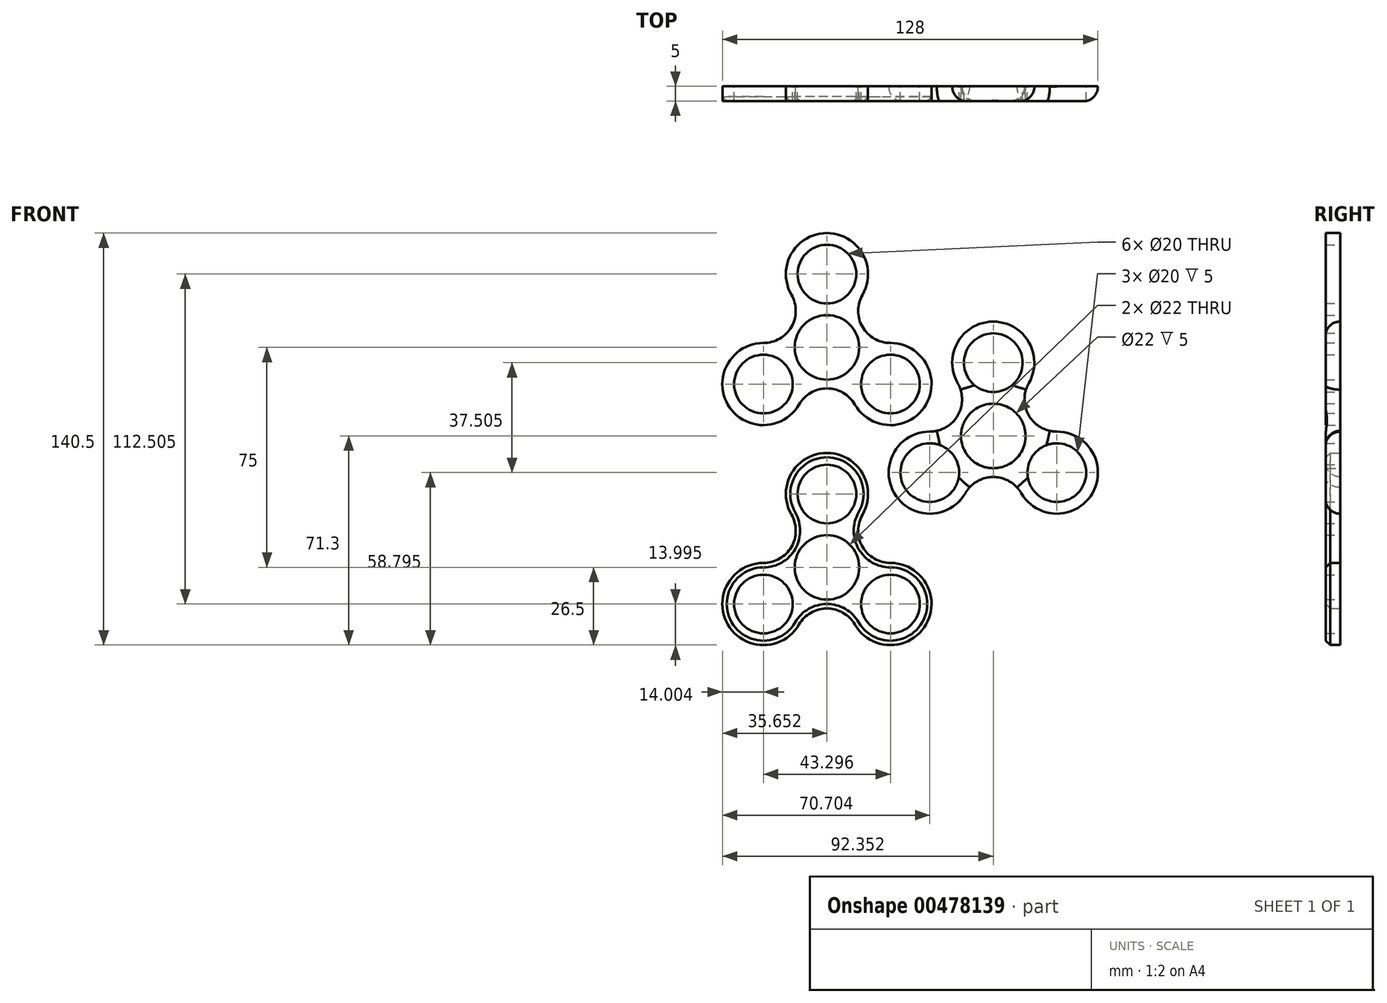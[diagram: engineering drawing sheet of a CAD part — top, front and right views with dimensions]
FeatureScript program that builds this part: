
annotation { "Feature Type Name" : "Feature", "Feature Type Description" : "" }
export const myFeature = defineFeature(function(context is Context, id is Id, definition is map)
    precondition{}
    {
        {
            var Q0;
            Q0=qCreatedBy(makeId("Front.planeOp"),FACE);
            var sketch = newSketch(context, id + "F0", { "sketchPlane" : qUnion([Q0])});
            skCircle(sketch, "E0", {"center": v(16.93, -40.24) * mm, "radius": 39 * mm});
            skCircle(sketch, "E1", {"center": v(16.93, -40.24) * mm, "radius": 11 * mm});
            skArc(sketch, "E2", {"start": v(16.93, -1.24) * mm, "mid": v(-16.84, -20.74) * mm, "end": v(-16.84, -59.75) * mm});
            skArc(sketch, "E3", {"start": v(-16.84, -59.75) * mm, "mid": v(16.93, -79.25) * mm, "end": v(50.7, -59.75) * mm});
            skLineSegment(sketch, "E4", {"start": v(-16.84, -59.75) * mm, "end": v(-13.37, -57.75) * mm});
            skLineSegment(sketch, "E5", {"start": v(16.93, -1.24) * mm, "end": v(16.93, -5.24) * mm});
            skLineSegment(sketch, "E6", {"start": v(50.7, -59.75) * mm, "end": v(47.24, -57.75) * mm});
            skCircle(sketch, "E7", {"center": v(16.93, -15.24) * mm, "radius": 10 * mm});
            skCircle(sketch, "E8", {"center": v(-4.72, -52.74) * mm, "radius": 10 * mm});
            skCircle(sketch, "E9", {"center": v(38.58, -52.74) * mm, "radius": 10 * mm});
            skCircle(sketch, "E10", {"center": v(16.93, -15.24) * mm, "radius": 14 * mm});
            skCircle(sketch, "E11", {"center": v(-4.72, -52.74) * mm, "radius": 14 * mm});
            skCircle(sketch, "E12", {"center": v(38.58, -52.74) * mm, "radius": 14 * mm});
            skPoint(sketch, "E13", {"position": v(16.93, -54.24) * mm});
            skPoint(sketch, "E14", {"position": v(4.6, -33.6) * mm});
            skPoint(sketch, "E15", {"position": v(28.85, -32.89) * mm});
            skArc(sketch, "E16", {"start": v(29.05, -22.25) * mm, "mid": v(29.05, -33.25) * mm, "end": v(38.57, -38.74) * mm});
            skArc(sketch, "E17", {"start": v(-4.7, -38.74) * mm, "mid": v(4.82, -33.25) * mm, "end": v(4.81, -22.25) * mm});
            skArc(sketch, "E18", {"start": v(26.45, -59.74) * mm, "mid": v(16.93, -54.24) * mm, "end": v(7.41, -59.74) * mm});
            skSolve(sketch);
        }
        {
            var Q0;
            {var subQ5=sQuery(id+"F0.wireOp",EDGE,"E16");Q0=makeQuery(id+"F0.imprint","IMPRINT",FACE,{"disambiguationData":[TD([[makeQuery(id+"F0.imprint","IMPRINT",EDGE,{"derivedFrom":subQ5}),-1.0]])]});}
            var Q1;
            Q1=makeQuery(id+"F0.imprint","IMPRINT",FACE,{"disambiguationData":[TD([[makeQuery(id+"F0.imprint","IMPRINT",EDGE,{"derivedFrom":sQuery(id+"F0.wireOp",EDGE,"E9")}),-1.0]])]});
            var Q2;
            {var subQ5=sQuery(id+"F0.wireOp",EDGE,"E18");Q2=makeQuery(id+"F0.imprint","IMPRINT",FACE,{"disambiguationData":[TD([[makeQuery(id+"F0.imprint","IMPRINT",EDGE,{"derivedFrom":subQ5}),-1.0]])]});}
            var Q3;
            Q3=makeQuery(id+"F0.imprint","IMPRINT",FACE,{"disambiguationData":[TD([[makeQuery(id+"F0.imprint","IMPRINT",EDGE,{"derivedFrom":sQuery(id+"F0.wireOp",EDGE,"E8")}),-1.0]])]});
            var Q4;
            {var subQ5=sQuery(id+"F0.wireOp",EDGE,"E17");Q4=makeQuery(id+"F0.imprint","IMPRINT",FACE,{"disambiguationData":[TD([[makeQuery(id+"F0.imprint","IMPRINT",EDGE,{"derivedFrom":subQ5}),-1.0]])]});}
            var Q5;
            Q5=makeQuery(id+"F0.imprint","IMPRINT",FACE,{"disambiguationData":[TD([[makeQuery(id+"F0.imprint","IMPRINT",EDGE,{"derivedFrom":sQuery(id+"F0.wireOp",EDGE,"E7")}),-1.0]])]});
            extrude(context, id + "F1", {"entities" : qUnion([Q0, Q1, Q2, Q3, Q4, Q5]), "depth" : 5 * mm});
        }
        {
            var Q0;
            Q0=qCreatedBy(makeId("Front.planeOp"),FACE);
            var sketch = newSketch(context, id + "F2", { "sketchPlane" : qUnion([Q0])});
            skLineSegment(sketch, "E19", {"start": v(-59.68, 64.11) * mm, "end": v(-59.68, -13.89) * mm});
            skLineSegment(sketch, "E20", {"start": v(-59.68, 64.11) * mm, "end": v(-59.68, 61.11) * mm});
            skLineSegment(sketch, "E21", {"start": v(-59.68, 61.11) * mm, "end": v(-59.68, 39.11) * mm});
            skLineSegment(sketch, "E22", {"start": v(-59.68, 39.11) * mm, "end": v(-59.68, 36.11) * mm});
            skLineSegment(sketch, "E23", {"start": v(-59.68, 36.11) * mm, "end": v(-59.68, 14.11) * mm});
            skLineSegment(sketch, "E24", {"start": v(-59.68, 14.11) * mm, "end": v(-59.68, 11.11) * mm});
            skLineSegment(sketch, "E25", {"start": v(-59.68, 11.11) * mm, "end": v(-59.68, -10.89) * mm});
            skLineSegment(sketch, "E26", {"start": v(-59.68, -10.89) * mm, "end": v(-59.68, -13.89) * mm});
            skCircle(sketch, "E27", {"center": v(-59.68, 50.11) * mm, "radius": 11 * mm});
            skCircle(sketch, "E28", {"center": v(-59.68, 25.11) * mm, "radius": 11 * mm});
            skCircle(sketch, "E29", {"center": v(-59.68, 0.11) * mm, "radius": 11 * mm});
            skCircle(sketch, "E30", {"center": v(-59.68, 0.11) * mm, "radius": 14 * mm});
            skCircle(sketch, "E31", {"center": v(-59.68, 25.11) * mm, "radius": 14 * mm});
            skCircle(sketch, "E32", {"center": v(-59.68, 50.11) * mm, "radius": 14 * mm});
            skArc(sketch, "E33", {"start": v(-48.31, 16.94) * mm, "mid": v(-49.7, 12.61) * mm, "end": v(-48.31, 8.28) * mm});
            skArc(sketch, "E34.MirrorCS", {"start": v(-71.05, 16.94) * mm, "mid": v(-69.66, 12.61) * mm, "end": v(-71.05, 8.28) * mm});
            skLineSegment(sketch, "E35", {"start": v(-70.68, 25.11) * mm, "end": v(-48.68, 25.11) * mm});
            skArc(sketch, "E36.MirrorCS", {"start": v(-48.31, 33.28) * mm, "mid": v(-49.7, 37.61) * mm, "end": v(-48.31, 41.94) * mm});
            skArc(sketch, "E37.MirrorCS", {"start": v(-71.05, 33.28) * mm, "mid": v(-69.66, 37.61) * mm, "end": v(-71.05, 41.94) * mm});
            skSolve(sketch);
        }
        {
            var Q0;
            {var subQ7=sQuery(id+"F2.wireOp",EDGE,"E20");Q0=makeQuery(id+"F2.imprint","IMPRINT",FACE,{"disambiguationData":[TD([[makeQuery(id+"F2.imprint","IMPRINT",EDGE,{"derivedFrom":subQ7}),1.0]])]});}
            var Q1;
            {var subQ0=sQuery(id+"F2.wireOp",EDGE,"E37.MirrorCS");Q1=makeQuery(id+"F2.imprint","IMPRINT",FACE,{"disambiguationData":[TD([[makeQuery(id+"F2.imprint","IMPRINT",EDGE,{"derivedFrom":subQ0}),-1.0]])]});}
            var Q2;
            {var subQ1=sQuery(id+"F2.wireOp",EDGE,"E20");Q2=makeQuery(id+"F2.imprint","IMPRINT",FACE,{"disambiguationData":[TD([[makeQuery(id+"F2.imprint","IMPRINT",EDGE,{"derivedFrom":subQ1}),-1.0]])]});}
            var Q3;
            {var subQ0=sQuery(id+"F2.wireOp",EDGE,"E22");Q3=makeQuery(id+"F2.imprint","IMPRINT",FACE,{"disambiguationData":[TD([[makeQuery(id+"F2.imprint","IMPRINT",EDGE,{"derivedFrom":subQ0}),-1.0]])]});}
            var Q4;
            {var subQ0=sQuery(id+"F2.wireOp",EDGE,"E22");Q4=makeQuery(id+"F2.imprint","IMPRINT",FACE,{"disambiguationData":[TD([[makeQuery(id+"F2.imprint","IMPRINT",EDGE,{"derivedFrom":subQ0}),1.0]])]});}
            var Q5;
            {var subQ0=sQuery(id+"F2.wireOp",EDGE,"E31");var subQ1=makeQuery(id+"F2.imprint","INTERSECT",VERTEX,{"derivedFrom":[subQ0,sQuery(id+"F2.wireOp",EDGE,"E36.MirrorCS")]});Q5=makeQuery(id+"F2.imprint","IMPRINT",FACE,{"disambiguationData":[TD([[makeQuery(id+"F2.imprint","IMPRINT",EDGE,{"disambiguationData":[TD([[subQ1,-1.0]])],"derivedFrom":subQ0}),1.0]])]});}
            var Q6;
            {var subQ0=sQuery(id+"F2.wireOp",EDGE,"E36.MirrorCS");Q6=makeQuery(id+"F2.imprint","IMPRINT",FACE,{"disambiguationData":[TD([[makeQuery(id+"F2.imprint","IMPRINT",EDGE,{"derivedFrom":subQ0}),1.0]])]});}
            var Q7;
            {var subQ0=sQuery(id+"F2.wireOp",EDGE,"E31");var subQ1=makeQuery(id+"F2.imprint","INTERSECT",VERTEX,{"derivedFrom":[subQ0,sQuery(id+"F2.wireOp",EDGE,"E37.MirrorCS")]});Q7=makeQuery(id+"F2.imprint","IMPRINT",FACE,{"disambiguationData":[TD([[makeQuery(id+"F2.imprint","IMPRINT",EDGE,{"disambiguationData":[TD([[subQ1,1.0]])],"derivedFrom":subQ0}),1.0]])]});}
            var Q8;
            {var subQ0=sQuery(id+"F2.wireOp",EDGE,"E24");Q8=makeQuery(id+"F2.imprint","IMPRINT",FACE,{"disambiguationData":[TD([[makeQuery(id+"F2.imprint","IMPRINT",EDGE,{"derivedFrom":subQ0}),-1.0]])]});}
            var Q9;
            {var subQ0=sQuery(id+"F2.wireOp",EDGE,"E24");Q9=makeQuery(id+"F2.imprint","IMPRINT",FACE,{"disambiguationData":[TD([[makeQuery(id+"F2.imprint","IMPRINT",EDGE,{"derivedFrom":subQ0}),1.0]])]});}
            var Q10;
            {var subQ0=sQuery(id+"F2.wireOp",EDGE,"E33");Q10=makeQuery(id+"F2.imprint","IMPRINT",FACE,{"disambiguationData":[TD([[makeQuery(id+"F2.imprint","IMPRINT",EDGE,{"derivedFrom":subQ0}),-1.0]])]});}
            var Q11;
            {var subQ1=sQuery(id+"F2.wireOp",EDGE,"E26");Q11=makeQuery(id+"F2.imprint","IMPRINT",FACE,{"disambiguationData":[TD([[makeQuery(id+"F2.imprint","IMPRINT",EDGE,{"derivedFrom":subQ1}),1.0]])]});}
            var Q12;
            {var subQ0=sQuery(id+"F2.wireOp",EDGE,"E34.MirrorCS");Q12=makeQuery(id+"F2.imprint","IMPRINT",FACE,{"disambiguationData":[TD([[makeQuery(id+"F2.imprint","IMPRINT",EDGE,{"derivedFrom":subQ0}),1.0]])]});}
            var Q13;
            {var subQ1=sQuery(id+"F2.wireOp",EDGE,"E26");Q13=makeQuery(id+"F2.imprint","IMPRINT",FACE,{"disambiguationData":[TD([[makeQuery(id+"F2.imprint","IMPRINT",EDGE,{"derivedFrom":subQ1}),-1.0]])]});}
            extrude(context, id + "F3", {"entities" : qUnion([Q0, Q1, Q2, Q3, Q4, Q5, Q6, Q7, Q8, Q9, Q10, Q11, Q12, Q13]), "depth" : 5 * mm});
        }
        {
            var Q0;
            Q0=makeQuery(id+"F3.opExtrude","CAP_EDGE",EDGE,{"disambiguationData":[OSD([sQuery(id+"F2.wireOp",EDGE,"E32")])],"isStart":false});
            var Q1;
            Q1=makeQuery(id+"F3.opExtrude","CAP_EDGE",EDGE,{"disambiguationData":[OSD([sQuery(id+"F2.wireOp",EDGE,"E37.MirrorCS")])],"isStart":false});
            var Q2;
            {var subQ0=sQuery(id+"F2.wireOp",EDGE,"E31");Q2=makeQuery(id+"F3.opExtrude","CAP_EDGE",EDGE,{"disambiguationData":[OSD([subQ0]),TDD([makeQuery(id+"F2.imprint","IMPRINT",EDGE,{"disambiguationData":[TD([[makeQuery(id+"F2.imprint","INTERSECT",VERTEX,{"derivedFrom":[subQ0,sQuery(id+"F2.wireOp",EDGE,"E34.MirrorCS")]}),1.0]])],"derivedFrom":subQ0})])],"isStart":false});}
            var Q3;
            Q3=makeQuery(id+"F3.opExtrude","CAP_EDGE",EDGE,{"disambiguationData":[OSD([sQuery(id+"F2.wireOp",EDGE,"E32")])],"isStart":true});
            var Q4;
            {var subQ0=sQuery(id+"F2.wireOp",EDGE,"E31");Q4=makeQuery(id+"F3.opExtrude","CAP_EDGE",EDGE,{"disambiguationData":[OSD([subQ0]),TDD([makeQuery(id+"F2.imprint","IMPRINT",EDGE,{"disambiguationData":[TD([[makeQuery(id+"F2.imprint","INTERSECT",VERTEX,{"derivedFrom":[subQ0,sQuery(id+"F2.wireOp",EDGE,"E33")]}),-1.0]])],"derivedFrom":subQ0})])],"isStart":true});}
            var Q5;
            Q5=makeQuery(id+"F3.opExtrude","CAP_EDGE",EDGE,{"disambiguationData":[OSD([sQuery(id+"F2.wireOp",EDGE,"E33")])],"isStart":true});
            var Q6;
            Q6=makeQuery(id+"F3.opExtrude","CAP_EDGE",EDGE,{"disambiguationData":[OSD([sQuery(id+"F2.wireOp",EDGE,"E30")])],"isStart":true});
            var Q7;
            Q7=makeQuery(id+"F3.opExtrude","CAP_EDGE",EDGE,{"disambiguationData":[OSD([sQuery(id+"F2.wireOp",EDGE,"E34.MirrorCS")])],"isStart":true});
            var Q8;
            {var subQ0=sQuery(id+"F2.wireOp",EDGE,"E31");Q8=makeQuery(id+"F3.opExtrude","CAP_EDGE",EDGE,{"disambiguationData":[OSD([subQ0]),TDD([makeQuery(id+"F2.imprint","IMPRINT",EDGE,{"disambiguationData":[TD([[makeQuery(id+"F2.imprint","INTERSECT",VERTEX,{"derivedFrom":[subQ0,sQuery(id+"F2.wireOp",EDGE,"E34.MirrorCS")]}),1.0]])],"derivedFrom":subQ0})])],"isStart":true});}
            var Q9;
            Q9=makeQuery(id+"F3.opExtrude","CAP_EDGE",EDGE,{"disambiguationData":[OSD([sQuery(id+"F2.wireOp",EDGE,"E37.MirrorCS")])],"isStart":true});
            var Q10;
            Q10=makeQuery(id+"F3.opExtrude","CAP_EDGE",EDGE,{"disambiguationData":[OSD([sQuery(id+"F2.wireOp",EDGE,"E36.MirrorCS")])],"isStart":true});
            var Q11;
            Q11=makeQuery(id+"F3.opExtrude","CAP_EDGE",EDGE,{"disambiguationData":[OSD([sQuery(id+"F2.wireOp",EDGE,"E36.MirrorCS")])],"isStart":false});
            var Q12;
            {var subQ0=sQuery(id+"F2.wireOp",EDGE,"E31");Q12=makeQuery(id+"F3.opExtrude","CAP_EDGE",EDGE,{"disambiguationData":[OSD([subQ0]),TDD([makeQuery(id+"F2.imprint","IMPRINT",EDGE,{"disambiguationData":[TD([[makeQuery(id+"F2.imprint","INTERSECT",VERTEX,{"derivedFrom":[subQ0,sQuery(id+"F2.wireOp",EDGE,"E33")]}),-1.0]])],"derivedFrom":subQ0})])],"isStart":false});}
            var Q13;
            Q13=makeQuery(id+"F3.opExtrude","CAP_EDGE",EDGE,{"disambiguationData":[OSD([sQuery(id+"F2.wireOp",EDGE,"E33")])],"isStart":false});
            var Q14;
            Q14=makeQuery(id+"F3.opExtrude","CAP_EDGE",EDGE,{"disambiguationData":[OSD([sQuery(id+"F2.wireOp",EDGE,"E30")])],"isStart":false});
            var Q15;
            Q15=makeQuery(id+"F3.opExtrude","CAP_EDGE",EDGE,{"disambiguationData":[OSD([sQuery(id+"F2.wireOp",EDGE,"E34.MirrorCS")])],"isStart":false});
            fillet(context, id + "F4", {"entities" : qUnion([Q0, Q1, Q2, Q3, Q4, Q5, Q6, Q7, Q8, Q9, Q10, Q11, Q12, Q13, Q14, Q15]), "radius" : 2.5 * mm, "tangentPropagation" : true, "allowEdgeOverflow" : false});
        }
        {
            var Q0;
            Q0=makeQuery(id+"F1.opExtrude","SWEPT_BODY",BODY,{"disambiguationData":[OSD([sQuery(id+"F0.wireOp",EDGE,"E1"),sQuery(id+"F0.wireOp",EDGE,"E7"),sQuery(id+"F0.wireOp",EDGE,"E8"),sQuery(id+"F0.wireOp",EDGE,"E9"),sQuery(id+"F0.wireOp",EDGE,"E10"),sQuery(id+"F0.wireOp",EDGE,"E11"),sQuery(id+"F0.wireOp",EDGE,"E12"),sQuery(id+"F0.wireOp",EDGE,"E16"),sQuery(id+"F0.wireOp",EDGE,"E17"),sQuery(id+"F0.wireOp",EDGE,"E18")])]});
            transform(context, id + "F5", {"entities" : qUnion([Q0]), "transformType" : TransformType.TRANSLATION_3D, "dx" : -4.7 * mm, "dy" : 0 * mm, "dz" : 62.9 * mm, "makeCopy" : true});
        }
        {
            var Q0;
            Q0=makeQuery(id+"F5.opPattern","COPY",BODY,{"derivedFrom":makeQuery(id+"F1.opExtrude","SWEPT_BODY",BODY,{"disambiguationData":[OSD([sQuery(id+"F0.wireOp",EDGE,"E1"),sQuery(id+"F0.wireOp",EDGE,"E7"),sQuery(id+"F0.wireOp",EDGE,"E8"),sQuery(id+"F0.wireOp",EDGE,"E9"),sQuery(id+"F0.wireOp",EDGE,"E10"),sQuery(id+"F0.wireOp",EDGE,"E11"),sQuery(id+"F0.wireOp",EDGE,"E12"),sQuery(id+"F0.wireOp",EDGE,"E16"),sQuery(id+"F0.wireOp",EDGE,"E17"),sQuery(id+"F0.wireOp",EDGE,"E18")])]}),"instanceName":"1"});
            transform(context, id + "F6", {"entities" : qUnion([Q0]), "transformType" : TransformType.TRANSLATION_3D, "dx" : -52 * mm, "dy" : 0 * mm, "dz" : -32.7 * mm, "makeCopy" : true});
        }
        {
            var Q0;
            Q0=makeQuery(id+"F3.opExtrude","SWEPT_BODY",BODY,{"disambiguationData":[OSD([sQuery(id+"F2.wireOp",EDGE,"E27"),sQuery(id+"F2.wireOp",EDGE,"E28"),sQuery(id+"F2.wireOp",EDGE,"E29"),sQuery(id+"F2.wireOp",EDGE,"E30"),sQuery(id+"F2.wireOp",EDGE,"E31"),sQuery(id+"F2.wireOp",EDGE,"E32"),sQuery(id+"F2.wireOp",EDGE,"E33"),sQuery(id+"F2.wireOp",EDGE,"E34.MirrorCS"),sQuery(id+"F2.wireOp",EDGE,"E36.MirrorCS"),sQuery(id+"F2.wireOp",EDGE,"E37.MirrorCS")])]});
            deleteBodies(context, id + "F7", {"entities" : qUnion([Q0])});
        }
        {
            var Q0;
            Q0=makeQuery(id+"F1.opExtrude","CAP_EDGE",EDGE,{"disambiguationData":[OSD([sQuery(id+"F0.wireOp",EDGE,"E12")])],"isStart":false});
            fillet(context, id + "F8", {"entities" : qUnion([Q0]), "radius" : 5 * mm, "tangentPropagation" : true, "allowEdgeOverflow" : false});
        }
        {
            var Q0;
            Q0=makeQuery(id+"F5.opPattern","COPY",EDGE,{"derivedFrom":makeQuery(id+"F1.opExtrude","CAP_EDGE",EDGE,{"disambiguationData":[OSD([sQuery(id+"F0.wireOp",EDGE,"E18")])],"isStart":false}),"instanceName":"1"});
            chamfer(context, id + "F9", {"entities" : qUnion([Q0]), "width" : 4 * mm, "tangentPropagation" : true});
        }
        {
            var Q0;
            Q0=makeQuery(id+"F5.opPattern","COPY",BODY,{"derivedFrom":makeQuery(id+"F1.opExtrude","SWEPT_BODY",BODY,{"disambiguationData":[OSD([sQuery(id+"F0.wireOp",EDGE,"E1"),sQuery(id+"F0.wireOp",EDGE,"E7"),sQuery(id+"F0.wireOp",EDGE,"E8"),sQuery(id+"F0.wireOp",EDGE,"E9"),sQuery(id+"F0.wireOp",EDGE,"E10"),sQuery(id+"F0.wireOp",EDGE,"E11"),sQuery(id+"F0.wireOp",EDGE,"E12"),sQuery(id+"F0.wireOp",EDGE,"E16"),sQuery(id+"F0.wireOp",EDGE,"E17"),sQuery(id+"F0.wireOp",EDGE,"E18")])]}),"instanceName":"1"});
            deleteBodies(context, id + "F10", {"entities" : qUnion([Q0])});
        }
        {
            var Q0;
            Q0=makeQuery(id+"F6.opPattern","COPY",BODY,{"derivedFrom":makeQuery(id+"F5.opPattern","COPY",BODY,{"derivedFrom":makeQuery(id+"F1.opExtrude","SWEPT_BODY",BODY,{"disambiguationData":[OSD([sQuery(id+"F0.wireOp",EDGE,"E1"),sQuery(id+"F0.wireOp",EDGE,"E7"),sQuery(id+"F0.wireOp",EDGE,"E8"),sQuery(id+"F0.wireOp",EDGE,"E9"),sQuery(id+"F0.wireOp",EDGE,"E10"),sQuery(id+"F0.wireOp",EDGE,"E11"),sQuery(id+"F0.wireOp",EDGE,"E12"),sQuery(id+"F0.wireOp",EDGE,"E16"),sQuery(id+"F0.wireOp",EDGE,"E17"),sQuery(id+"F0.wireOp",EDGE,"E18")])]}),"instanceName":"1"}),"instanceName":"1"});
            transform(context, id + "F11", {"entities" : qUnion([Q0]), "transformType" : TransformType.TRANSLATION_3D, "dx" : 0 * mm, "dy" : 0 * mm, "dz" : -75 * mm, "makeCopy" : true});
        }
        {
            var Q0;
            Q0=makeQuery(id+"F11.opPattern","COPY",EDGE,{"derivedFrom":makeQuery(id+"F6.opPattern","COPY",EDGE,{"derivedFrom":makeQuery(id+"F5.opPattern","COPY",EDGE,{"derivedFrom":makeQuery(id+"F1.opExtrude","CAP_EDGE",EDGE,{"disambiguationData":[OSD([sQuery(id+"F0.wireOp",EDGE,"E12")])],"isStart":false}),"instanceName":"1"}),"instanceName":"1"}),"instanceName":"1"});
            var Q1;
            Q1=makeQuery(id+"F11.opPattern","COPY",EDGE,{"derivedFrom":makeQuery(id+"F6.opPattern","COPY",EDGE,{"derivedFrom":makeQuery(id+"F5.opPattern","COPY",EDGE,{"derivedFrom":makeQuery(id+"F1.opExtrude","CAP_EDGE",EDGE,{"disambiguationData":[OSD([sQuery(id+"F0.wireOp",EDGE,"E11")])],"isStart":false}),"instanceName":"1"}),"instanceName":"1"}),"instanceName":"1"});
            var Q2;
            Q2=makeQuery(id+"F11.opPattern","COPY",EDGE,{"derivedFrom":makeQuery(id+"F6.opPattern","COPY",EDGE,{"derivedFrom":makeQuery(id+"F5.opPattern","COPY",EDGE,{"derivedFrom":makeQuery(id+"F1.opExtrude","CAP_EDGE",EDGE,{"disambiguationData":[OSD([sQuery(id+"F0.wireOp",EDGE,"E10")])],"isStart":false}),"instanceName":"1"}),"instanceName":"1"}),"instanceName":"1"});
            var Q3;
            Q3=makeQuery(id+"F11.opPattern","COPY",EDGE,{"derivedFrom":makeQuery(id+"F6.opPattern","COPY",EDGE,{"derivedFrom":makeQuery(id+"F5.opPattern","COPY",EDGE,{"derivedFrom":makeQuery(id+"F1.opExtrude","CAP_EDGE",EDGE,{"disambiguationData":[OSD([sQuery(id+"F0.wireOp",EDGE,"E17")])],"isStart":false}),"instanceName":"1"}),"instanceName":"1"}),"instanceName":"1"});
            var Q4;
            Q4=makeQuery(id+"F11.opPattern","COPY",EDGE,{"derivedFrom":makeQuery(id+"F6.opPattern","COPY",EDGE,{"derivedFrom":makeQuery(id+"F5.opPattern","COPY",EDGE,{"derivedFrom":makeQuery(id+"F1.opExtrude","CAP_EDGE",EDGE,{"disambiguationData":[OSD([sQuery(id+"F0.wireOp",EDGE,"E16")])],"isStart":false}),"instanceName":"1"}),"instanceName":"1"}),"instanceName":"1"});
            var Q5;
            Q5=makeQuery(id+"F11.opPattern","COPY",EDGE,{"derivedFrom":makeQuery(id+"F6.opPattern","COPY",EDGE,{"derivedFrom":makeQuery(id+"F5.opPattern","COPY",EDGE,{"derivedFrom":makeQuery(id+"F1.opExtrude","CAP_EDGE",EDGE,{"disambiguationData":[OSD([sQuery(id+"F0.wireOp",EDGE,"E18")])],"isStart":false}),"instanceName":"1"}),"instanceName":"1"}),"instanceName":"1"});
            chamfer(context, id + "F12", {"entities" : qUnion([Q0, Q1, Q2, Q3, Q4, Q5]), "width" : 1.5 * mm, "tangentPropagation" : true});
        }
    });
